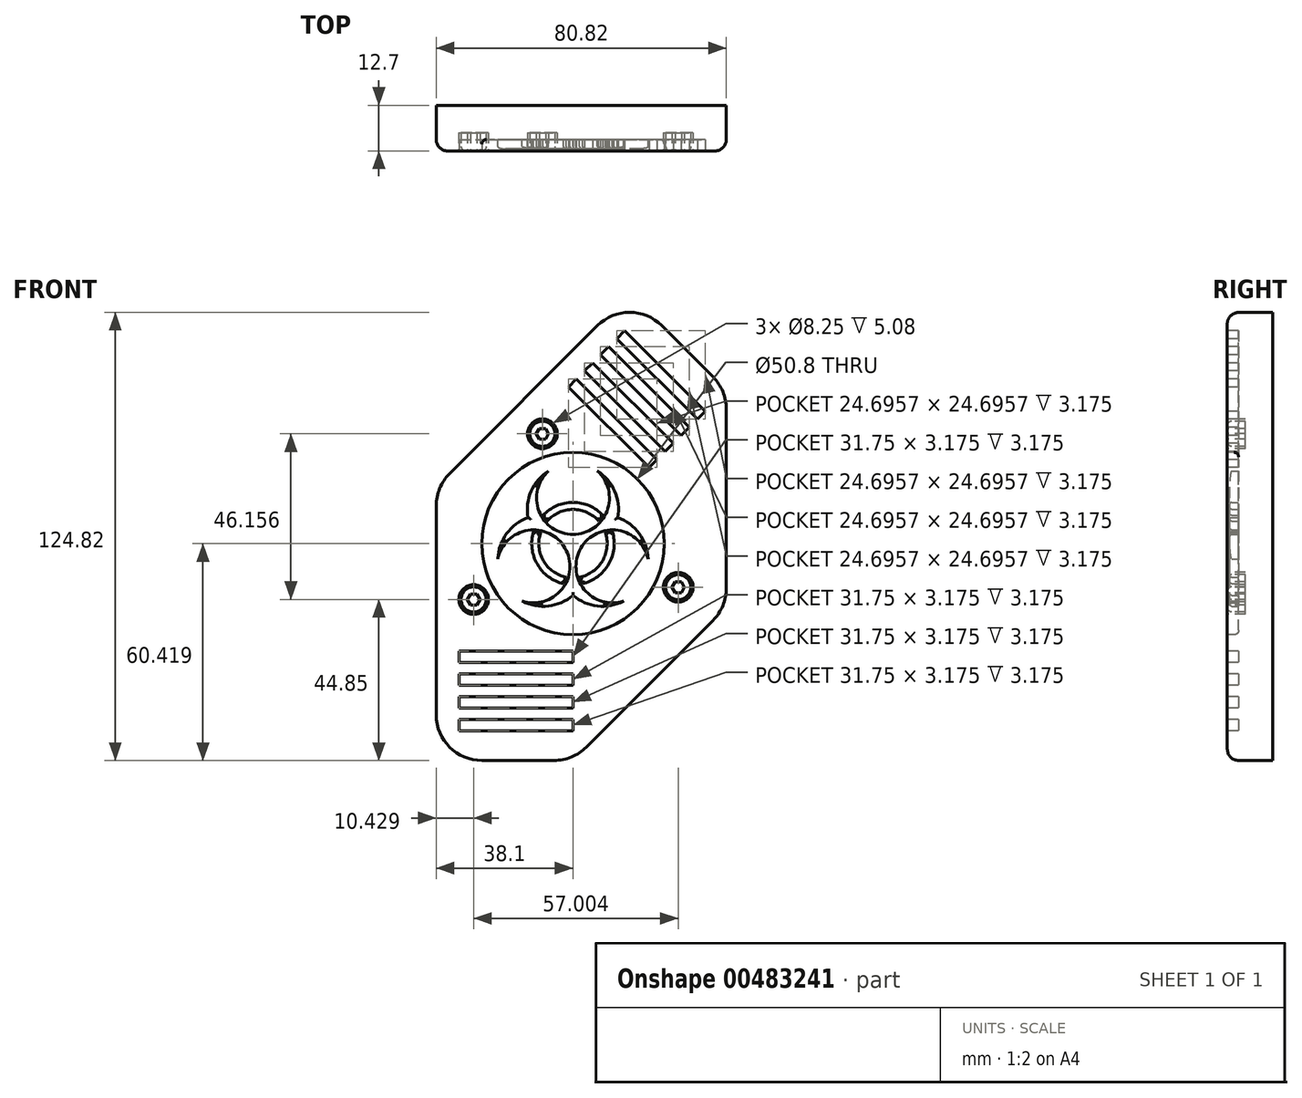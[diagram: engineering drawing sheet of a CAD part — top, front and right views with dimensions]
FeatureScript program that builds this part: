
annotation { "Feature Type Name" : "Feature", "Feature Type Description" : "" }
export const myFeature = defineFeature(function(context is Context, id is Id, definition is map)
    precondition{}
    {
        {
            var Q0;
            Q0=qCreatedBy(makeId("Front.planeOp"),FACE);
            var sketch = newSketch(context, id + "F0", { "sketchPlane" : qUnion([Q0])});
            skLineSegment(sketch, "E0", {"start": v(0, 12.7) * mm, "end": v(0, 70.94) * mm});
            skLineSegment(sketch, "E1", {"start": v(3.72, 79.92) * mm, "end": v(44.9, 121.1) * mm});
            skLineSegment(sketch, "E2", {"start": v(62.86, 121.1) * mm, "end": v(77.1, 106.86) * mm});
            skLineSegment(sketch, "E3", {"start": v(32.84, 0) * mm, "end": v(12.7, 0) * mm});
            skLineSegment(sketch, "E4", {"start": v(80.82, 97.88) * mm, "end": v(80.82, 47.98) * mm});
            skLineSegment(sketch, "E5", {"start": v(41.82, 3.72) * mm, "end": v(77.1, 39) * mm});
            skPoint(sketch, "E6.visualSharp", {"position": v(53.88, 130.08) * mm});
            skArc(sketch, "E6.filletArc", {"start": v(62.86, 121.1) * mm, "mid": v(53.88, 124.82) * mm, "end": v(44.9, 121.1) * mm});
            skPoint(sketch, "E7.visualSharp", {"position": v(80.82, 103.14) * mm});
            skArc(sketch, "E7.filletArc", {"start": v(80.82, 97.88) * mm, "mid": v(79.86, 102.74) * mm, "end": v(77.1, 106.86) * mm});
            skPoint(sketch, "E8.visualSharp", {"position": v(80.82, 42.72) * mm});
            skArc(sketch, "E8.filletArc", {"start": v(77.1, 39) * mm, "mid": v(79.86, 43.12) * mm, "end": v(80.82, 47.98) * mm});
            skPoint(sketch, "E9.visualSharp", {"position": v(38.1, 0) * mm});
            skArc(sketch, "E9.filletArc", {"start": v(32.84, 0) * mm, "mid": v(37.7, 0.97) * mm, "end": v(41.82, 3.72) * mm});
            skPoint(sketch, "E10.visualSharp", {"position": v(0, 0) * mm});
            skArc(sketch, "E10.filletArc", {"start": v(0, 12.7) * mm, "mid": v(3.72, 3.72) * mm, "end": v(12.7, 0) * mm});
            skPoint(sketch, "E11.visualSharp", {"position": v(0, 76.2) * mm});
            skArc(sketch, "E11.filletArc", {"start": v(3.72, 79.92) * mm, "mid": v(0.97, 75.8) * mm, "end": v(0, 70.94) * mm});
            skSolve(sketch);
        }
        {
            var Q0;
            Q0 = qSketchRegion(id + "F0", true);
            extrude(context, id + "F1", {"entities" : qUnion([Q0]), "depth" : 12.7 * mm});
        }
        {
            var Q0;
            Q0=makeQuery(id+"F1.opExtrude","CAP_FACE",FACE,{"disambiguationData":[OSD([sQuery(id+"F0.wireOp",EDGE,"E0"),sQuery(id+"F0.wireOp",EDGE,"E1"),sQuery(id+"F0.wireOp",EDGE,"E2"),sQuery(id+"F0.wireOp",EDGE,"E3"),sQuery(id+"F0.wireOp",EDGE,"E4"),sQuery(id+"F0.wireOp",EDGE,"E5"),sQuery(id+"F0.wireOp",EDGE,"E6.filletArc"),sQuery(id+"F0.wireOp",EDGE,"E7.filletArc"),sQuery(id+"F0.wireOp",EDGE,"E8.filletArc"),sQuery(id+"F0.wireOp",EDGE,"E9.filletArc"),sQuery(id+"F0.wireOp",EDGE,"E10.filletArc"),sQuery(id+"F0.wireOp",EDGE,"E11.filletArc")])],"isStart":false});
            fillet(context, id + "F2", {"entities" : qUnion([Q0]), "radius" : 3.17 * mm, "tangentPropagation" : true, "allowEdgeOverflow" : false});
        }
        {
            var Q0;
            Q0=makeQuery(id+"F1.opExtrude","CAP_FACE",FACE,{"disambiguationData":[OSD([sQuery(id+"F0.wireOp",EDGE,"E0"),sQuery(id+"F0.wireOp",EDGE,"E1"),sQuery(id+"F0.wireOp",EDGE,"E2"),sQuery(id+"F0.wireOp",EDGE,"E3"),sQuery(id+"F0.wireOp",EDGE,"E4"),sQuery(id+"F0.wireOp",EDGE,"E5"),sQuery(id+"F0.wireOp",EDGE,"E6.filletArc"),sQuery(id+"F0.wireOp",EDGE,"E7.filletArc"),sQuery(id+"F0.wireOp",EDGE,"E8.filletArc"),sQuery(id+"F0.wireOp",EDGE,"E9.filletArc"),sQuery(id+"F0.wireOp",EDGE,"E10.filletArc"),sQuery(id+"F0.wireOp",EDGE,"E11.filletArc")])],"isStart":false});
            var sketch = newSketch(context, id + "F3", { "sketchPlane" : qUnion([Q0])});
            skCircle(sketch, "E12", {"center": v(38.1, 60.42) * mm, "radius": 25.4 * mm});
            skSolve(sketch);
        }
        {
            var Q0;
            Q0 = qSketchRegion(id + "F3", true);
            extrude(context, id + "F4", {"entities" : qUnion([Q0]), "operationType" : NewBodyOperationType.REMOVE, "oppositeDirection" : true, "depth" : 3.17 * mm});
        }
        {
            var Q0;
            Q0=makeQuery(id+"F1.opExtrude","CAP_FACE",FACE,{"disambiguationData":[OSD([sQuery(id+"F0.wireOp",EDGE,"E0"),sQuery(id+"F0.wireOp",EDGE,"E1"),sQuery(id+"F0.wireOp",EDGE,"E2"),sQuery(id+"F0.wireOp",EDGE,"E3"),sQuery(id+"F0.wireOp",EDGE,"E4"),sQuery(id+"F0.wireOp",EDGE,"E5"),sQuery(id+"F0.wireOp",EDGE,"E6.filletArc"),sQuery(id+"F0.wireOp",EDGE,"E7.filletArc"),sQuery(id+"F0.wireOp",EDGE,"E8.filletArc"),sQuery(id+"F0.wireOp",EDGE,"E9.filletArc"),sQuery(id+"F0.wireOp",EDGE,"E10.filletArc"),sQuery(id+"F0.wireOp",EDGE,"E11.filletArc")])],"isStart":false});
            var sketch = newSketch(context, id + "F5", { "sketchPlane" : qUnion([Q0])});
            skLineSegment(sketch, "E13", {"start": v(36.82, 104.04) * mm, "end": v(39.06, 106.28) * mm});
            skLineSegment(sketch, "E14", {"start": v(39.06, 106.28) * mm, "end": v(61.51, 83.83) * mm});
            skLineSegment(sketch, "E15", {"start": v(61.51, 83.83) * mm, "end": v(59.27, 81.59) * mm});
            skLineSegment(sketch, "E16", {"start": v(59.27, 81.59) * mm, "end": v(36.82, 104.04) * mm});
            skLineSegment(sketch, "E17.1.0.0", {"start": v(63.76, 86.08) * mm, "end": v(41.3, 108.53) * mm});
            skLineSegment(sketch, "E17.1.0.1", {"start": v(43.55, 110.77) * mm, "end": v(66, 88.32) * mm});
            skLineSegment(sketch, "E17.1.0.2", {"start": v(66, 88.32) * mm, "end": v(63.76, 86.08) * mm});
            skLineSegment(sketch, "E17.1.0.3", {"start": v(41.3, 108.53) * mm, "end": v(43.55, 110.77) * mm});
            skLineSegment(sketch, "E17.2.0.0", {"start": v(68.25, 90.57) * mm, "end": v(45.8, 113.02) * mm});
            skLineSegment(sketch, "E17.2.0.1", {"start": v(48.04, 115.26) * mm, "end": v(70.5, 92.81) * mm});
            skLineSegment(sketch, "E17.2.0.2", {"start": v(70.5, 92.81) * mm, "end": v(68.25, 90.57) * mm});
            skLineSegment(sketch, "E17.2.0.3", {"start": v(45.8, 113.02) * mm, "end": v(48.04, 115.26) * mm});
            skLineSegment(sketch, "E17.3.0.0", {"start": v(72.74, 95.06) * mm, "end": v(50.29, 117.5) * mm});
            skLineSegment(sketch, "E17.3.0.1", {"start": v(52.53, 119.75) * mm, "end": v(74.99, 97.3) * mm});
            skLineSegment(sketch, "E17.3.0.2", {"start": v(74.99, 97.3) * mm, "end": v(72.74, 95.06) * mm});
            skLineSegment(sketch, "E17.3.0.3", {"start": v(50.29, 117.5) * mm, "end": v(52.53, 119.75) * mm});
            skLineSegment(sketch, "E17.direction1", {"start": v(59.27, 81.59) * mm, "end": v(63.76, 86.08) * mm, "construction": true});
            skLineSegment(sketch, "E18.bottom", {"start": v(6.35, 30.48) * mm, "end": v(38.1, 30.48) * mm});
            skLineSegment(sketch, "E18.top", {"start": v(6.35, 27.3) * mm, "end": v(38.1, 27.3) * mm});
            skLineSegment(sketch, "E18.left", {"start": v(6.35, 30.48) * mm, "end": v(6.35, 27.3) * mm});
            skLineSegment(sketch, "E18.right", {"start": v(38.1, 30.48) * mm, "end": v(38.1, 27.3) * mm});
            skLineSegment(sketch, "E19.0.1.0", {"start": v(6.35, 24.13) * mm, "end": v(38.1, 24.13) * mm});
            skLineSegment(sketch, "E19.0.1.1", {"start": v(6.35, 20.95) * mm, "end": v(38.1, 20.95) * mm});
            skLineSegment(sketch, "E19.0.1.2", {"start": v(6.35, 24.13) * mm, "end": v(6.35, 20.95) * mm});
            skLineSegment(sketch, "E19.0.1.3", {"start": v(38.1, 24.13) * mm, "end": v(38.1, 20.95) * mm});
            skLineSegment(sketch, "E19.0.2.0", {"start": v(6.35, 17.78) * mm, "end": v(38.1, 17.78) * mm});
            skLineSegment(sketch, "E19.0.2.1", {"start": v(6.35, 14.6) * mm, "end": v(38.1, 14.6) * mm});
            skLineSegment(sketch, "E19.0.2.2", {"start": v(6.35, 17.78) * mm, "end": v(6.35, 14.6) * mm});
            skLineSegment(sketch, "E19.0.2.3", {"start": v(38.1, 17.78) * mm, "end": v(38.1, 14.6) * mm});
            skLineSegment(sketch, "E19.0.3.0", {"start": v(6.35, 11.43) * mm, "end": v(38.1, 11.43) * mm});
            skLineSegment(sketch, "E19.0.3.1", {"start": v(6.35, 8.25) * mm, "end": v(38.1, 8.25) * mm});
            skLineSegment(sketch, "E19.0.3.2", {"start": v(6.35, 11.43) * mm, "end": v(6.35, 8.25) * mm});
            skLineSegment(sketch, "E19.0.3.3", {"start": v(38.1, 11.43) * mm, "end": v(38.1, 8.25) * mm});
            skLineSegment(sketch, "E19.direction1", {"start": v(6.35, 27.3) * mm, "end": v(31.75, 27.3) * mm, "construction": true});
            skLineSegment(sketch, "E19.direction2", {"start": v(6.35, 27.3) * mm, "end": v(6.35, 20.95) * mm, "construction": true});
            skSolve(sketch);
        }
        {
            var Q0;
            Q0 = qSketchRegion(id + "F5", true);
            extrude(context, id + "F6", {"entities" : qUnion([Q0]), "operationType" : NewBodyOperationType.REMOVE, "oppositeDirection" : true, "depth" : 3.17 * mm});
        }
        {
            var Q0;
            Q0=makeQuery(id+"F1.opExtrude","CAP_FACE",FACE,{"disambiguationData":[OSD([sQuery(id+"F0.wireOp",EDGE,"E0"),sQuery(id+"F0.wireOp",EDGE,"E1"),sQuery(id+"F0.wireOp",EDGE,"E2"),sQuery(id+"F0.wireOp",EDGE,"E3"),sQuery(id+"F0.wireOp",EDGE,"E4"),sQuery(id+"F0.wireOp",EDGE,"E5"),sQuery(id+"F0.wireOp",EDGE,"E6.filletArc"),sQuery(id+"F0.wireOp",EDGE,"E7.filletArc"),sQuery(id+"F0.wireOp",EDGE,"E8.filletArc"),sQuery(id+"F0.wireOp",EDGE,"E9.filletArc"),sQuery(id+"F0.wireOp",EDGE,"E10.filletArc"),sQuery(id+"F0.wireOp",EDGE,"E11.filletArc")])],"isStart":false});
            var sketch = newSketch(context, id + "F7", { "sketchPlane" : qUnion([Q0])});
            skLineSegment(sketch, "E20", {"start": v(76.92, 44.34) * mm, "end": v(3.9, 74.58) * mm, "construction": true});
            skLineSegment(sketch, "E21", {"start": v(3.17, 41.82) * mm, "end": v(77.65, 72.93) * mm, "construction": true});
            skLineSegment(sketch, "E22", {"start": v(26.56, 98.27) * mm, "end": v(57.59, 23.98) * mm, "construction": true});
            skCircle(sketch, "E23.0", {"center": v(38.1, 60.42) * mm, "radius": 31.75 * mm, "construction": true});
            skCircle(sketch, "E24", {"center": v(10.43, 44.85) * mm, "radius": 4.12 * mm});
            skCircle(sketch, "E25", {"center": v(29.59, 91) * mm, "radius": 4.12 * mm});
            skCircle(sketch, "E26", {"center": v(67.43, 48.27) * mm, "radius": 4.12 * mm});
            skCircle(sketch, "E27", {"center": v(10.43, 44.85) * mm, "radius": 3.5 * mm});
            skCircle(sketch, "E28", {"center": v(29.59, 91) * mm, "radius": 3.5 * mm});
            skCircle(sketch, "E29", {"center": v(67.43, 48.27) * mm, "radius": 3.5 * mm});
            skCircle(sketch, "E30.cCircle", {"center": v(10.43, 44.85) * mm, "radius": 1.5 * mm, "construction": true});
            skLineSegment(sketch, "E30.0", {"start": v(9.56, 46.35) * mm, "end": v(11.3, 46.35) * mm});
            skLineSegment(sketch, "E30.1", {"start": v(11.3, 46.35) * mm, "end": v(12.16, 44.85) * mm});
            skLineSegment(sketch, "E30.2", {"start": v(12.16, 44.85) * mm, "end": v(11.3, 43.35) * mm});
            skLineSegment(sketch, "E30.3", {"start": v(11.3, 43.35) * mm, "end": v(9.56, 43.35) * mm});
            skLineSegment(sketch, "E30.4", {"start": v(9.56, 43.35) * mm, "end": v(8.7, 44.85) * mm});
            skLineSegment(sketch, "E30.5", {"start": v(8.7, 44.85) * mm, "end": v(9.56, 46.35) * mm});
            skPoint(sketch, "E30.0.midPoint", {"position": v(10.43, 46.35) * mm});
            skCircle(sketch, "E31.cCircle", {"center": v(67.43, 48.27) * mm, "radius": 1.5 * mm, "construction": true});
            skLineSegment(sketch, "E31.0", {"start": v(66.57, 49.77) * mm, "end": v(68.3, 49.77) * mm});
            skLineSegment(sketch, "E31.1", {"start": v(68.3, 49.77) * mm, "end": v(69.17, 48.27) * mm});
            skLineSegment(sketch, "E31.2", {"start": v(69.17, 48.27) * mm, "end": v(68.3, 46.77) * mm});
            skLineSegment(sketch, "E31.3", {"start": v(68.3, 46.77) * mm, "end": v(66.57, 46.77) * mm});
            skLineSegment(sketch, "E31.4", {"start": v(66.57, 46.77) * mm, "end": v(65.7, 48.27) * mm});
            skLineSegment(sketch, "E31.5", {"start": v(65.7, 48.27) * mm, "end": v(66.57, 49.77) * mm});
            skPoint(sketch, "E31.0.midPoint", {"position": v(67.43, 49.77) * mm});
            skCircle(sketch, "E32.cCircle", {"center": v(29.59, 91) * mm, "radius": 1.5 * mm, "construction": true});
            skLineSegment(sketch, "E32.0", {"start": v(28.72, 92.5) * mm, "end": v(30.45, 92.5) * mm});
            skLineSegment(sketch, "E32.1", {"start": v(30.45, 92.5) * mm, "end": v(31.32, 91) * mm});
            skLineSegment(sketch, "E32.2", {"start": v(31.32, 91) * mm, "end": v(30.45, 89.5) * mm});
            skLineSegment(sketch, "E32.3", {"start": v(30.45, 89.5) * mm, "end": v(28.72, 89.5) * mm});
            skLineSegment(sketch, "E32.4", {"start": v(28.72, 89.5) * mm, "end": v(27.86, 91) * mm});
            skLineSegment(sketch, "E32.5", {"start": v(27.86, 91) * mm, "end": v(28.72, 92.5) * mm});
            skPoint(sketch, "E32.0.midPoint", {"position": v(29.59, 92.5) * mm});
            skSolve(sketch);
        }
        {
            var Q0;
            Q0 = qSketchRegion(id + "F7", true);
            extrude(context, id + "F8", {"entities" : qUnion([Q0]), "operationType" : NewBodyOperationType.REMOVE, "oppositeDirection" : true, "depth" : 5.08 * mm});
        }
        {
            var Q0;
            {var subQ0=sQuery(id+"F0.wireOp",EDGE,"E9.filletArc");var subQ1=sQuery(id+"F0.wireOp",EDGE,"E8.filletArc");var subQ2=sQuery(id+"F0.wireOp",EDGE,"E7.filletArc");var subQ3=sQuery(id+"F0.wireOp",EDGE,"E5");var subQ4=sQuery(id+"F0.wireOp",EDGE,"E4");var subQ5=sQuery(id+"F0.wireOp",EDGE,"E0");var subQ6=sQuery(id+"F0.wireOp",EDGE,"E1");var subQ7=sQuery(id+"F0.wireOp",EDGE,"E2");var subQ8=sQuery(id+"F0.wireOp",EDGE,"E3");var subQ9=sQuery(id+"F0.wireOp",EDGE,"E10.filletArc");var subQ10=sQuery(id+"F0.wireOp",EDGE,"E11.filletArc");var subQ11=sQuery(id+"F0.wireOp",EDGE,"E6.filletArc");Q0=makeQuery(id+"F8.boolean.opBoolean","SPLIT",FACE,{"disambiguationData":[TD([makeQuery(id+"F2.opFillet","BLEND_FACE",FACE,{"disambiguationData":[OSD([subQ5])]})])],"derivedFrom":makeQuery(id+"F1.opExtrude","CAP_FACE",FACE,{"disambiguationData":[OSD([subQ5,subQ6,subQ7,subQ8,subQ4,subQ3,subQ11,subQ2,subQ1,subQ0,subQ9,subQ10])],"isStart":false})});}
            var sketch = newSketch(context, id + "F9", { "sketchPlane" : qUnion([Q0])});
            skCircle(sketch, "E33.cCircle", {"center": v(29.59, 91) * mm, "radius": 1.5 * mm, "construction": true});
            skLineSegment(sketch, "E33.0", {"start": v(28.72, 92.5) * mm, "end": v(30.45, 92.5) * mm});
            skLineSegment(sketch, "E33.1", {"start": v(30.45, 92.5) * mm, "end": v(31.32, 91) * mm});
            skLineSegment(sketch, "E33.2", {"start": v(31.32, 91) * mm, "end": v(30.45, 89.5) * mm});
            skLineSegment(sketch, "E33.3", {"start": v(30.45, 89.5) * mm, "end": v(28.72, 89.5) * mm});
            skLineSegment(sketch, "E33.4", {"start": v(28.72, 89.5) * mm, "end": v(27.86, 91) * mm});
            skLineSegment(sketch, "E33.5", {"start": v(27.86, 91) * mm, "end": v(28.72, 92.5) * mm});
            skPoint(sketch, "E33.0.midPoint", {"position": v(29.59, 92.5) * mm});
            skCircle(sketch, "E34.cCircle", {"center": v(10.43, 44.85) * mm, "radius": 1.5 * mm, "construction": true});
            skLineSegment(sketch, "E34.0", {"start": v(9.56, 46.35) * mm, "end": v(11.3, 46.35) * mm});
            skLineSegment(sketch, "E34.1", {"start": v(11.3, 46.35) * mm, "end": v(12.16, 44.85) * mm});
            skLineSegment(sketch, "E34.2", {"start": v(12.16, 44.85) * mm, "end": v(11.3, 43.35) * mm});
            skLineSegment(sketch, "E34.3", {"start": v(11.3, 43.35) * mm, "end": v(9.56, 43.35) * mm});
            skLineSegment(sketch, "E34.4", {"start": v(9.56, 43.35) * mm, "end": v(8.7, 44.85) * mm});
            skLineSegment(sketch, "E34.5", {"start": v(8.7, 44.85) * mm, "end": v(9.56, 46.35) * mm});
            skPoint(sketch, "E34.0.midPoint", {"position": v(10.43, 46.35) * mm});
            skCircle(sketch, "E35.cCircle", {"center": v(67.43, 48.27) * mm, "radius": 1.5 * mm, "construction": true});
            skLineSegment(sketch, "E35.0", {"start": v(66.57, 49.77) * mm, "end": v(68.3, 49.77) * mm});
            skLineSegment(sketch, "E35.1", {"start": v(68.3, 49.77) * mm, "end": v(69.17, 48.27) * mm});
            skLineSegment(sketch, "E35.2", {"start": v(69.17, 48.27) * mm, "end": v(68.3, 46.77) * mm});
            skLineSegment(sketch, "E35.3", {"start": v(68.3, 46.77) * mm, "end": v(66.57, 46.77) * mm});
            skLineSegment(sketch, "E35.4", {"start": v(66.57, 46.77) * mm, "end": v(65.7, 48.27) * mm});
            skLineSegment(sketch, "E35.5", {"start": v(65.7, 48.27) * mm, "end": v(66.57, 49.77) * mm});
            skPoint(sketch, "E35.0.midPoint", {"position": v(67.43, 49.77) * mm});
            skSolve(sketch);
        }
        {
            var Q0;
            Q0 = qSketchRegion(id + "F9", true);
            extrude(context, id + "F10", {"entities" : qUnion([Q0]), "operationType" : NewBodyOperationType.REMOVE, "oppositeDirection" : true, "depth" : 5.08 * mm});
        }
        {
            var Q0;
            Q0=makeQuery(id+"F8.boolean.opBoolean","COPY",EDGE,{"derivedFrom":makeQuery(id+"F8.opExtrude","CAP_EDGE",EDGE,{"disambiguationData":[OSD([sQuery(id+"F7.wireOp",EDGE,"E28")])],"isStart":true})});
            var Q1;
            Q1=makeQuery(id+"F8.boolean.opBoolean","COPY",EDGE,{"derivedFrom":makeQuery(id+"F8.opExtrude","CAP_EDGE",EDGE,{"disambiguationData":[OSD([sQuery(id+"F7.wireOp",EDGE,"E27")])],"isStart":true})});
            var Q2;
            Q2=makeQuery(id+"F8.boolean.opBoolean","COPY",EDGE,{"derivedFrom":makeQuery(id+"F8.opExtrude","CAP_EDGE",EDGE,{"disambiguationData":[OSD([sQuery(id+"F7.wireOp",EDGE,"E29")])],"isStart":true})});
            var Q3;
            Q3=makeQuery(id+"F4.boolean.opBoolean","COPY",EDGE,{"derivedFrom":makeQuery(id+"F4.opExtrude","CAP_EDGE",EDGE,{"disambiguationData":[OSD([sQuery(id+"F3.wireOp",EDGE,"E12")])],"isStart":true})});
            var Q4;
            Q4=makeQuery(id+"F4.boolean.opBoolean","COPY",EDGE,{"derivedFrom":makeQuery(id+"F4.opExtrude","CAP_EDGE",EDGE,{"disambiguationData":[OSD([sQuery(id+"F3.wireOp",EDGE,"E12")])],"isStart":false})});
            var Q5;
            Q5=makeQuery(id+"F6.boolean.opBoolean","COPY",EDGE,{"derivedFrom":makeQuery(id+"F6.opExtrude","CAP_EDGE",EDGE,{"disambiguationData":[OSD([sQuery(id+"F5.wireOp",EDGE,"E16")])],"isStart":true})});
            var Q6;
            Q6=makeQuery(id+"F6.boolean.opBoolean","COPY",EDGE,{"derivedFrom":makeQuery(id+"F6.opExtrude","CAP_EDGE",EDGE,{"disambiguationData":[OSD([sQuery(id+"F5.wireOp",EDGE,"E13")])],"isStart":true})});
            var Q7;
            Q7=makeQuery(id+"F6.boolean.opBoolean","COPY",EDGE,{"derivedFrom":makeQuery(id+"F6.opExtrude","CAP_EDGE",EDGE,{"disambiguationData":[OSD([sQuery(id+"F5.wireOp",EDGE,"E14")])],"isStart":true})});
            var Q8;
            Q8=makeQuery(id+"F6.boolean.opBoolean","COPY",EDGE,{"derivedFrom":makeQuery(id+"F6.opExtrude","CAP_EDGE",EDGE,{"disambiguationData":[OSD([sQuery(id+"F5.wireOp",EDGE,"E15")])],"isStart":true})});
            var Q9;
            Q9=makeQuery(id+"F6.boolean.opBoolean","COPY",EDGE,{"derivedFrom":makeQuery(id+"F6.opExtrude","CAP_EDGE",EDGE,{"disambiguationData":[OSD([sQuery(id+"F5.wireOp",EDGE,"E17.1.0.3")])],"isStart":true})});
            var Q10;
            Q10=makeQuery(id+"F6.boolean.opBoolean","COPY",EDGE,{"derivedFrom":makeQuery(id+"F6.opExtrude","CAP_EDGE",EDGE,{"disambiguationData":[OSD([sQuery(id+"F5.wireOp",EDGE,"E17.2.0.3")])],"isStart":true})});
            var Q11;
            Q11=makeQuery(id+"F6.boolean.opBoolean","COPY",EDGE,{"derivedFrom":makeQuery(id+"F6.opExtrude","CAP_EDGE",EDGE,{"disambiguationData":[OSD([sQuery(id+"F5.wireOp",EDGE,"E17.3.0.3")])],"isStart":true})});
            var Q12;
            Q12=makeQuery(id+"F6.boolean.opBoolean","COPY",EDGE,{"derivedFrom":makeQuery(id+"F6.opExtrude","CAP_EDGE",EDGE,{"disambiguationData":[OSD([sQuery(id+"F5.wireOp",EDGE,"E17.1.0.2")])],"isStart":true})});
            var Q13;
            Q13=makeQuery(id+"F6.boolean.opBoolean","COPY",EDGE,{"derivedFrom":makeQuery(id+"F6.opExtrude","CAP_EDGE",EDGE,{"disambiguationData":[OSD([sQuery(id+"F5.wireOp",EDGE,"E17.2.0.2")])],"isStart":true})});
            var Q14;
            Q14=makeQuery(id+"F6.boolean.opBoolean","COPY",EDGE,{"derivedFrom":makeQuery(id+"F6.opExtrude","CAP_EDGE",EDGE,{"disambiguationData":[OSD([sQuery(id+"F5.wireOp",EDGE,"E17.3.0.2")])],"isStart":true})});
            var Q15;
            Q15=makeQuery(id+"F6.boolean.opBoolean","COPY",EDGE,{"derivedFrom":makeQuery(id+"F6.opExtrude","CAP_EDGE",EDGE,{"disambiguationData":[OSD([sQuery(id+"F5.wireOp",EDGE,"E17.1.0.0")])],"isStart":true})});
            var Q16;
            Q16=makeQuery(id+"F6.boolean.opBoolean","COPY",EDGE,{"derivedFrom":makeQuery(id+"F6.opExtrude","CAP_EDGE",EDGE,{"disambiguationData":[OSD([sQuery(id+"F5.wireOp",EDGE,"E17.1.0.1")])],"isStart":true})});
            var Q17;
            Q17=makeQuery(id+"F6.boolean.opBoolean","COPY",EDGE,{"derivedFrom":makeQuery(id+"F6.opExtrude","CAP_EDGE",EDGE,{"disambiguationData":[OSD([sQuery(id+"F5.wireOp",EDGE,"E17.2.0.0")])],"isStart":true})});
            var Q18;
            Q18=makeQuery(id+"F6.boolean.opBoolean","COPY",EDGE,{"derivedFrom":makeQuery(id+"F6.opExtrude","CAP_EDGE",EDGE,{"disambiguationData":[OSD([sQuery(id+"F5.wireOp",EDGE,"E17.2.0.1")])],"isStart":true})});
            var Q19;
            Q19=makeQuery(id+"F6.boolean.opBoolean","COPY",EDGE,{"derivedFrom":makeQuery(id+"F6.opExtrude","CAP_EDGE",EDGE,{"disambiguationData":[OSD([sQuery(id+"F5.wireOp",EDGE,"E17.3.0.0")])],"isStart":true})});
            var Q20;
            Q20=makeQuery(id+"F6.boolean.opBoolean","COPY",EDGE,{"derivedFrom":makeQuery(id+"F6.opExtrude","CAP_EDGE",EDGE,{"disambiguationData":[OSD([sQuery(id+"F5.wireOp",EDGE,"E17.3.0.1")])],"isStart":true})});
            var Q21;
            Q21=makeQuery(id+"F6.boolean.opBoolean","COPY",EDGE,{"derivedFrom":makeQuery(id+"F6.opExtrude","CAP_EDGE",EDGE,{"disambiguationData":[OSD([sQuery(id+"F5.wireOp",EDGE,"E18.left")])],"isStart":true})});
            var Q22;
            Q22=makeQuery(id+"F6.boolean.opBoolean","COPY",EDGE,{"derivedFrom":makeQuery(id+"F6.opExtrude","CAP_EDGE",EDGE,{"disambiguationData":[OSD([sQuery(id+"F5.wireOp",EDGE,"E18.bottom")])],"isStart":true})});
            var Q23;
            Q23=makeQuery(id+"F6.boolean.opBoolean","COPY",EDGE,{"derivedFrom":makeQuery(id+"F6.opExtrude","CAP_EDGE",EDGE,{"disambiguationData":[OSD([sQuery(id+"F5.wireOp",EDGE,"E19.0.1.2")])],"isStart":true})});
            var Q24;
            Q24=makeQuery(id+"F6.boolean.opBoolean","COPY",EDGE,{"derivedFrom":makeQuery(id+"F6.opExtrude","CAP_EDGE",EDGE,{"disambiguationData":[OSD([sQuery(id+"F5.wireOp",EDGE,"E19.0.2.2")])],"isStart":true})});
            var Q25;
            Q25=makeQuery(id+"F6.boolean.opBoolean","COPY",EDGE,{"derivedFrom":makeQuery(id+"F6.opExtrude","CAP_EDGE",EDGE,{"disambiguationData":[OSD([sQuery(id+"F5.wireOp",EDGE,"E19.0.3.2")])],"isStart":true})});
            var Q26;
            Q26=makeQuery(id+"F6.boolean.opBoolean","COPY",EDGE,{"derivedFrom":makeQuery(id+"F6.opExtrude","CAP_EDGE",EDGE,{"disambiguationData":[OSD([sQuery(id+"F5.wireOp",EDGE,"E19.0.3.3")])],"isStart":true})});
            var Q27;
            Q27=makeQuery(id+"F6.boolean.opBoolean","COPY",EDGE,{"derivedFrom":makeQuery(id+"F6.opExtrude","CAP_EDGE",EDGE,{"disambiguationData":[OSD([sQuery(id+"F5.wireOp",EDGE,"E19.0.2.3")])],"isStart":true})});
            var Q28;
            Q28=makeQuery(id+"F6.boolean.opBoolean","COPY",EDGE,{"derivedFrom":makeQuery(id+"F6.opExtrude","CAP_EDGE",EDGE,{"disambiguationData":[OSD([sQuery(id+"F5.wireOp",EDGE,"E19.0.1.3")])],"isStart":true})});
            var Q29;
            Q29=makeQuery(id+"F6.boolean.opBoolean","COPY",EDGE,{"derivedFrom":makeQuery(id+"F6.opExtrude","CAP_EDGE",EDGE,{"disambiguationData":[OSD([sQuery(id+"F5.wireOp",EDGE,"E18.right")])],"isStart":true})});
            var Q30;
            Q30=makeQuery(id+"F6.boolean.opBoolean","COPY",EDGE,{"derivedFrom":makeQuery(id+"F6.opExtrude","CAP_EDGE",EDGE,{"disambiguationData":[OSD([sQuery(id+"F5.wireOp",EDGE,"E18.top")])],"isStart":true})});
            var Q31;
            Q31=makeQuery(id+"F6.boolean.opBoolean","COPY",EDGE,{"derivedFrom":makeQuery(id+"F6.opExtrude","CAP_EDGE",EDGE,{"disambiguationData":[OSD([sQuery(id+"F5.wireOp",EDGE,"E19.0.1.0")])],"isStart":true})});
            var Q32;
            Q32=makeQuery(id+"F6.boolean.opBoolean","COPY",EDGE,{"derivedFrom":makeQuery(id+"F6.opExtrude","CAP_EDGE",EDGE,{"disambiguationData":[OSD([sQuery(id+"F5.wireOp",EDGE,"E19.0.1.1")])],"isStart":true})});
            var Q33;
            Q33=makeQuery(id+"F6.boolean.opBoolean","COPY",EDGE,{"derivedFrom":makeQuery(id+"F6.opExtrude","CAP_EDGE",EDGE,{"disambiguationData":[OSD([sQuery(id+"F5.wireOp",EDGE,"E19.0.2.0")])],"isStart":true})});
            var Q34;
            Q34=makeQuery(id+"F6.boolean.opBoolean","COPY",EDGE,{"derivedFrom":makeQuery(id+"F6.opExtrude","CAP_EDGE",EDGE,{"disambiguationData":[OSD([sQuery(id+"F5.wireOp",EDGE,"E19.0.2.1")])],"isStart":true})});
            var Q35;
            Q35=makeQuery(id+"F6.boolean.opBoolean","COPY",EDGE,{"derivedFrom":makeQuery(id+"F6.opExtrude","CAP_EDGE",EDGE,{"disambiguationData":[OSD([sQuery(id+"F5.wireOp",EDGE,"E19.0.3.0")])],"isStart":true})});
            var Q36;
            Q36=makeQuery(id+"F6.boolean.opBoolean","COPY",EDGE,{"derivedFrom":makeQuery(id+"F6.opExtrude","CAP_EDGE",EDGE,{"disambiguationData":[OSD([sQuery(id+"F5.wireOp",EDGE,"E19.0.3.1")])],"isStart":true})});
            fillet(context, id + "F11", {"entities" : qUnion([Q0, Q1, Q2, Q3, Q4, Q5, Q6, Q7, Q8, Q9, Q10, Q11, Q12, Q13, Q14, Q15, Q16, Q17, Q18, Q19, Q20, Q21, Q22, Q23, Q24, Q25, Q26, Q27, Q28, Q29, Q30, Q31, Q32, Q33, Q34, Q35, Q36]), "radius" : 1.27 * mm, "tangentPropagation" : true, "allowEdgeOverflow" : false});
        }
        {
            var Q0;
            Q0=makeQuery(id+"F4.boolean.opBoolean","COPY",FACE,{"derivedFrom":makeQuery(id+"F4.opExtrude","CAP_FACE",FACE,{"disambiguationData":[OSD([sQuery(id+"F3.wireOp",EDGE,"E12")])],"isStart":false})});
            var sketch = newSketch(context, id + "F12", { "sketchPlane" : qUnion([Q0])});
            skCircle(sketch, "E36.cCircle", {"center": v(38.1, 60.42) * mm, "radius": 25.4 * mm, "construction": true});
            skLineSegment(sketch, "E36.1", {"start": v(52.76, 85.82) * mm, "end": v(67.43, 60.42) * mm, "construction": true});
            skLineSegment(sketch, "E36.2", {"start": v(67.43, 60.42) * mm, "end": v(52.76, 35.02) * mm, "construction": true});
            skLineSegment(sketch, "E36.3", {"start": v(52.76, 35.02) * mm, "end": v(23.44, 35.02) * mm, "construction": true});
            skLineSegment(sketch, "E36.4", {"start": v(23.44, 35.02) * mm, "end": v(8.77, 60.42) * mm, "construction": true});
            skLineSegment(sketch, "E36.5", {"start": v(8.77, 60.42) * mm, "end": v(23.44, 85.82) * mm, "construction": true});
            skPoint(sketch, "E36.0.midPoint", {"position": v(38.1, 85.82) * mm});
            skLineSegment(sketch, "E37", {"start": v(38.1, 60.42) * mm, "end": v(60.1, 47.72) * mm, "construction": true});
            skLineSegment(sketch, "E38", {"start": v(38.1, 85.82) * mm, "end": v(38.1, 60.42) * mm, "construction": true});
            skLineSegment(sketch, "E39", {"start": v(38.1, 60.42) * mm, "end": v(16.1, 47.72) * mm, "construction": true});
            skArc(sketch, "E40", {"start": v(29.1, 63.51) * mm, "mid": v(29.85, 55.66) * mm, "end": v(36.28, 51.07) * mm});
            skArc(sketch, "E41", {"start": v(31.3, 80.67) * mm, "mid": v(26.46, 75.02) * mm, "end": v(25.61, 67.63) * mm});
            skArc(sketch, "E42", {"start": v(59.04, 56.17) * mm, "mid": v(56.57, 63.2) * mm, "end": v(50.59, 67.63) * mm});
            skArc(sketch, "E43", {"start": v(25.61, 67.63) * mm, "mid": v(19.63, 63.2) * mm, "end": v(17.16, 56.17) * mm});
            skCircle(sketch, "E44", {"center": v(38.1, 60.42) * mm, "radius": 12.7 * mm, "construction": true});
            skArc(sketch, "E45", {"start": v(31.3, 80.67) * mm, "mid": v(27.95, 73.63) * mm, "end": v(30.59, 66.28) * mm});
            skArc(sketch, "E46", {"start": v(23.95, 44.4) * mm, "mid": v(31.74, 45.03) * mm, "end": v(36.78, 50.99) * mm});
            skArc(sketch, "E47", {"start": v(59.04, 56.17) * mm, "mid": v(54.61, 62.6) * mm, "end": v(46.93, 64) * mm});
            skArc(sketch, "E48.trimOffspring", {"start": v(23.95, 44.4) * mm, "mid": v(31.27, 43.04) * mm, "end": v(38.1, 46) * mm});
            skArc(sketch, "E49.trimOffspring", {"start": v(38.1, 46) * mm, "mid": v(44.93, 43.04) * mm, "end": v(52.25, 44.4) * mm});
            skArc(sketch, "E50.trimOffspring", {"start": v(50.59, 67.63) * mm, "mid": v(49.74, 75.02) * mm, "end": v(44.9, 80.67) * mm});
            skArc(sketch, "E51", {"start": v(27.1, 63.72) * mm, "mid": v(28.15, 54.68) * mm, "end": v(35.46, 49.24) * mm});
            skArc(sketch, "E52.trimOffspring", {"start": v(30.59, 66.28) * mm, "mid": v(38.1, 62.96) * mm, "end": v(45.61, 66.28) * mm});
            skArc(sketch, "E53.trimOffspring", {"start": v(29.27, 64) * mm, "mid": v(21.59, 62.6) * mm, "end": v(17.16, 56.17) * mm});
            skArc(sketch, "E54.trimOffspring", {"start": v(45.28, 66.67) * mm, "mid": v(38.1, 69.94) * mm, "end": v(30.92, 66.67) * mm});
            skArc(sketch, "E55.trimOffspring", {"start": v(46.46, 68.3) * mm, "mid": v(38.1, 71.9) * mm, "end": v(29.74, 68.3) * mm});
            skArc(sketch, "E56.trimOffspring", {"start": v(45.61, 66.28) * mm, "mid": v(48.25, 73.63) * mm, "end": v(44.9, 80.67) * mm});
            skArc(sketch, "E57.trimOffspring", {"start": v(46.93, 64) * mm, "mid": v(40.3, 59.15) * mm, "end": v(39.42, 50.99) * mm});
            skArc(sketch, "E58.trimOffspring", {"start": v(39.92, 51.07) * mm, "mid": v(46.35, 55.66) * mm, "end": v(47.1, 63.51) * mm});
            skArc(sketch, "E59.trimOffspring", {"start": v(40.74, 49.24) * mm, "mid": v(48.05, 54.68) * mm, "end": v(49.1, 63.72) * mm});
            skArc(sketch, "E60.trimOffspring", {"start": v(36.78, 50.99) * mm, "mid": v(35.9, 59.15) * mm, "end": v(29.27, 64) * mm});
            skArc(sketch, "E61.trimOffspring", {"start": v(39.42, 50.99) * mm, "mid": v(44.46, 45.03) * mm, "end": v(52.25, 44.4) * mm});
            skLineSegment(sketch, "E62", {"start": v(38.1, 60.42) * mm, "end": v(16.1, 73.12) * mm, "construction": true});
            skLineSegment(sketch, "E63", {"start": v(38.1, 60.42) * mm, "end": v(60.1, 73.12) * mm, "construction": true});
            skLineSegment(sketch, "E64", {"start": v(38.1, 60.42) * mm, "end": v(38.1, 35.02) * mm, "construction": true});
            skArc(sketch, "E65", {"start": v(29.74, 68.3) * mm, "mid": v(30.29, 67.45) * mm, "end": v(30.92, 66.67) * mm});
            skArc(sketch, "E66", {"start": v(46.46, 68.3) * mm, "mid": v(45.91, 67.45) * mm, "end": v(45.28, 66.67) * mm});
            skArc(sketch, "E67", {"start": v(27.1, 63.72) * mm, "mid": v(28.1, 63.67) * mm, "end": v(29.1, 63.51) * mm});
            skArc(sketch, "E68", {"start": v(35.46, 49.24) * mm, "mid": v(35.92, 50.13) * mm, "end": v(36.28, 51.07) * mm});
            skArc(sketch, "E69", {"start": v(40.74, 49.24) * mm, "mid": v(40.28, 50.13) * mm, "end": v(39.92, 51.07) * mm});
            skArc(sketch, "E70", {"start": v(49.1, 63.72) * mm, "mid": v(48.1, 63.67) * mm, "end": v(47.1, 63.51) * mm});
            skSolve(sketch);
        }
        {
            var Q0;
            Q0 = qSketchRegion(id + "F12", true);
            extrude(context, id + "F13", {"entities" : qUnion([Q0]), "operationType" : NewBodyOperationType.ADD, "depth" : 2.54 * mm});
        }
        {
            var Q0;
            Q0=makeQuery(id+"F13.opExtrude","CAP_FACE",FACE,{"disambiguationData":[OSD([sQuery(id+"F12.wireOp",EDGE,"E41"),sQuery(id+"F12.wireOp",EDGE,"E42"),sQuery(id+"F12.wireOp",EDGE,"E43"),sQuery(id+"F12.wireOp",EDGE,"E45"),sQuery(id+"F12.wireOp",EDGE,"E46"),sQuery(id+"F12.wireOp",EDGE,"E47"),sQuery(id+"F12.wireOp",EDGE,"E48.trimOffspring"),sQuery(id+"F12.wireOp",EDGE,"E49.trimOffspring"),sQuery(id+"F12.wireOp",EDGE,"E50.trimOffspring"),sQuery(id+"F12.wireOp",EDGE,"E52.trimOffspring"),sQuery(id+"F12.wireOp",EDGE,"E53.trimOffspring"),sQuery(id+"F12.wireOp",EDGE,"E56.trimOffspring"),sQuery(id+"F12.wireOp",EDGE,"E57.trimOffspring"),sQuery(id+"F12.wireOp",EDGE,"E60.trimOffspring"),sQuery(id+"F12.wireOp",EDGE,"E61.trimOffspring")])],"isStart":false});
            var Q1;
            Q1=makeQuery(id+"F13.opExtrude","CAP_FACE",FACE,{"disambiguationData":[OSD([sQuery(id+"F12.wireOp",EDGE,"E58.trimOffspring"),sQuery(id+"F12.wireOp",EDGE,"E59.trimOffspring"),sQuery(id+"F12.wireOp",EDGE,"E69"),sQuery(id+"F12.wireOp",EDGE,"E70")])],"isStart":false});
            var Q2;
            Q2=makeQuery(id+"F13.opExtrude","CAP_FACE",FACE,{"disambiguationData":[OSD([sQuery(id+"F12.wireOp",EDGE,"E54.trimOffspring"),sQuery(id+"F12.wireOp",EDGE,"E55.trimOffspring"),sQuery(id+"F12.wireOp",EDGE,"E65"),sQuery(id+"F12.wireOp",EDGE,"E66")])],"isStart":false});
            var Q3;
            Q3=makeQuery(id+"F13.opExtrude","CAP_FACE",FACE,{"disambiguationData":[OSD([sQuery(id+"F12.wireOp",EDGE,"E40"),sQuery(id+"F12.wireOp",EDGE,"E51"),sQuery(id+"F12.wireOp",EDGE,"E67"),sQuery(id+"F12.wireOp",EDGE,"E68")])],"isStart":false});
            fillet(context, id + "F14", {"entities" : qUnion([Q0, Q1, Q2, Q3]), "radius" : 0.64 * mm, "tangentPropagation" : true, "allowEdgeOverflow" : false});
        }
    });
